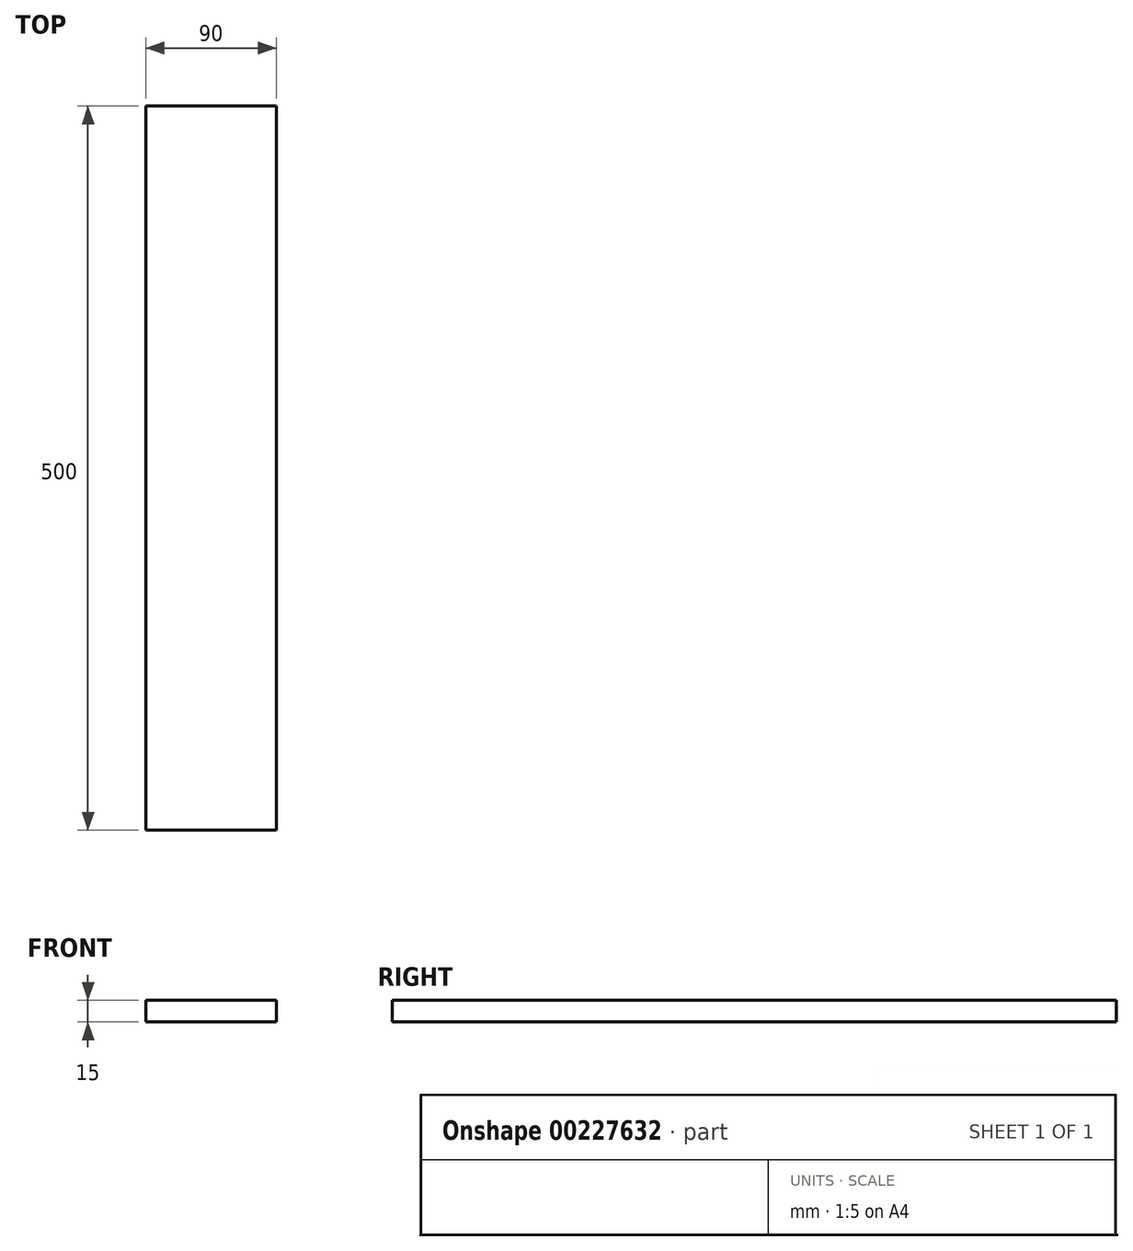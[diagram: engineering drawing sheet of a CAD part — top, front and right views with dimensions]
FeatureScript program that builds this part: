
annotation { "Feature Type Name" : "Feature", "Feature Type Description" : "" }
export const myFeature = defineFeature(function(context is Context, id is Id, definition is map)
    precondition{}
    {
        {
            var Q0;
            Q0=qCreatedBy(makeId("Front.planeOp"),FACE);
            var sketch = newSketch(context, id + "F0", { "sketchPlane" : qUnion([Q0])});
            skLineSegment(sketch, "E0.bottom", {"start": v(-40.43, 3.08) * mm, "end": v(49.57, 3.08) * mm});
            skLineSegment(sketch, "E0.top", {"start": v(-40.43, -11.92) * mm, "end": v(49.57, -11.92) * mm});
            skLineSegment(sketch, "E0.left", {"start": v(-40.43, 3.08) * mm, "end": v(-40.43, -11.92) * mm});
            skLineSegment(sketch, "E0.right", {"start": v(49.57, 3.08) * mm, "end": v(49.57, -11.92) * mm});
            skSolve(sketch);
        }
        {
            var Q0;
            Q0=makeQuery(id+"F0.imprint","IMPRINT",FACE,{"disambiguationData":[TD([[makeQuery(id+"F0.imprint","IMPRINT",EDGE,{"derivedFrom":sQuery(id+"F0.wireOp",EDGE,"E0.bottom")}),-1.0]])]});
            extrude(context, id + "F1", {"entities" : qUnion([Q0]), "oppositeDirection" : true, "depth" : 500 * mm});
        }
    });
